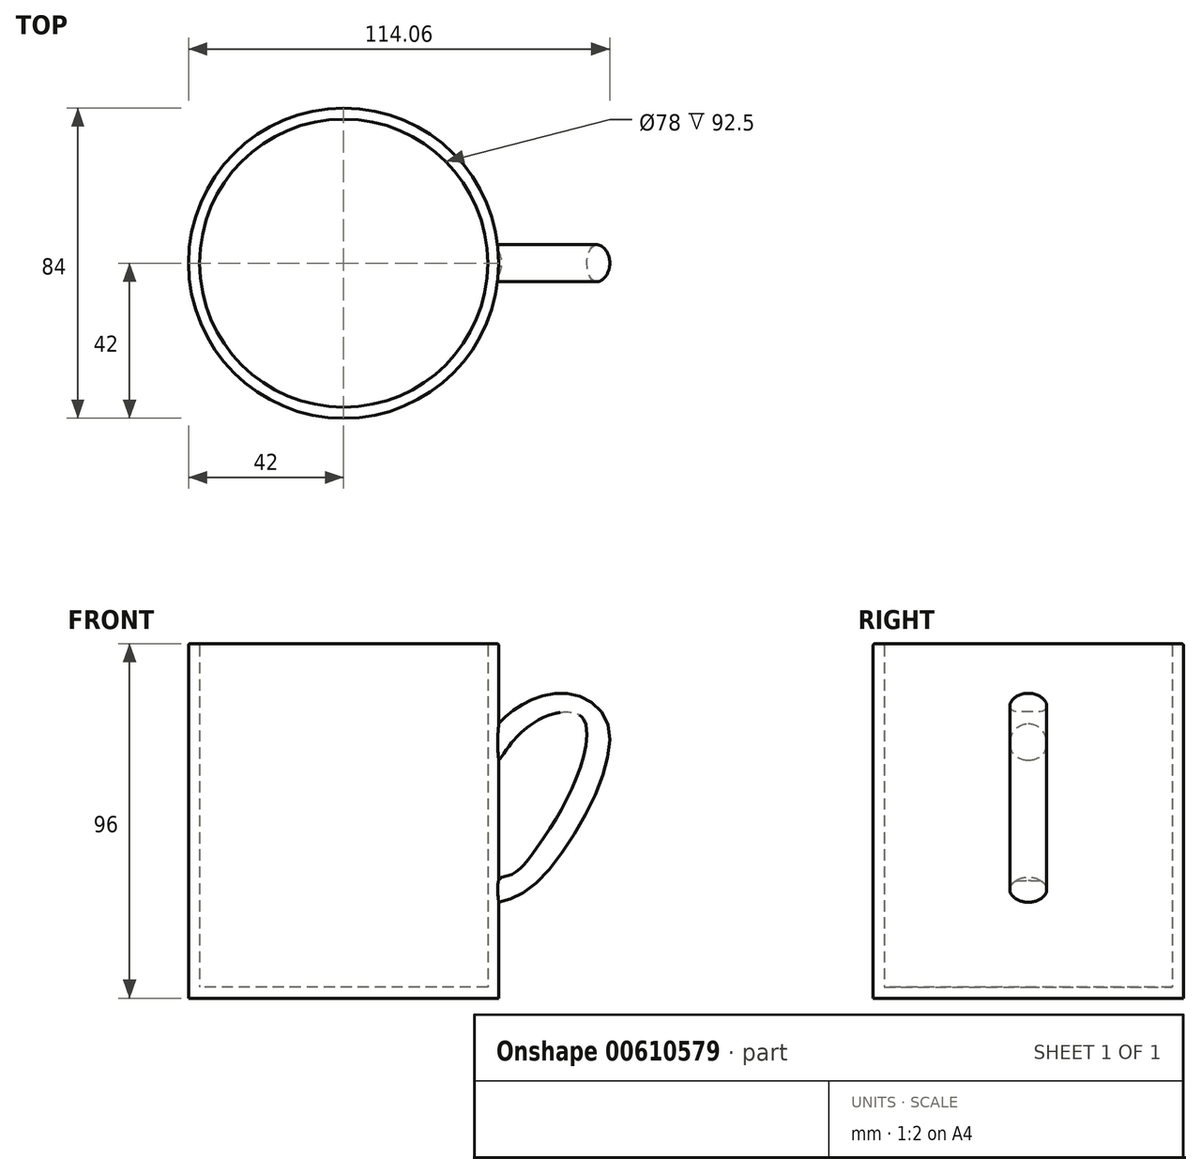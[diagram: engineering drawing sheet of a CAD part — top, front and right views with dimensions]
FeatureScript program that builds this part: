
annotation { "Feature Type Name" : "Feature", "Feature Type Description" : "" }
export const myFeature = defineFeature(function(context is Context, id is Id, definition is map)
    precondition{}
    {
        {
            var Q0;
            Q0=qCreatedBy(makeId("Top.planeOp"),FACE);
            var sketch = newSketch(context, id + "F0", { "sketchPlane" : qUnion([Q0])});
            skCircle(sketch, "E0", {"center": v(0, 0) * mm, "radius": 42 * mm});
            skSolve(sketch);
        }
        {
            var Q0;
            Q0 = qSketchRegion(id + "F0", true);
            extrude(context, id + "F1", {"entities" : qUnion([Q0]), "endBound" : BoundingType.SYMMETRIC, "depth" : 96 * mm, "offsetDistance" : 25 * mm});
        }
        {
            var Q0;
            Q0=qCreatedBy(makeId("Right.planeOp"),FACE);
            cPlane(context, id + "F2", {"entities" : qUnion([Q0]), "cplaneType" : CPlaneType.OFFSET, "offset" : 42 * mm, "width" : 150 * mm, "height" : 150 * mm});
        }
        {
            var Q0;
            Q0=qCreatedBy(makeId("Front.planeOp"),FACE);
            var sketch = newSketch(context, id + "F3", { "sketchPlane" : qUnion([Q0])});
            skFitSpline(sketch, "E1", {"points": [v(40.37, 21.1) * mm, v(47.45, 28.19) * mm, v(59.63, 32.15) * mm, v(69.54, 23.65) * mm, v(51.13, -14.59) * mm, v(38.38, -20.25) * mm], "startDerivative": vector(40.62, 48.6) * mm, "endDerivative": vector(-65.26, -9.16) * mm});
            skSolve(sketch);
        }
        {
            var Q0;
            Q0=qCreatedBy(id+"F2.planeOp",FACE);
            var sketch = newSketch(context, id + "F4", { "sketchPlane" : qUnion([Q0])});
            skCircle(sketch, "E2", {"center": v(0, 21.36) * mm, "radius": 5 * mm});
            skSolve(sketch);
        }
        {
            var Q0;
            Q0=makeQuery(id+"F4.imprint","IMPRINT",FACE,{"disambiguationData":[TD([[makeQuery(id+"F4.imprint","IMPRINT",EDGE,{"derivedFrom":sQuery(id+"F4.wireOp",EDGE,"E2")}),1.0]])]});
            var Q1;
            Q1=sQuery(id+"F3.wireOp",EDGE,"E1");
            sweep(context, id + "F5", {"operationType" : NewBodyOperationType.ADD, "profiles" : qUnion([Q0]), "path" : qUnion([Q1])});
        }
        {
            var Q0;
            Q0=makeQuery(id+"F1.opExtrude","CAP_FACE",FACE,{"disambiguationData":[OSD([sQuery(id+"F0.wireOp",EDGE,"E0")])],"isStart":false});
            shell(context, id + "F6", {"entities" : qUnion([Q0]), "thickness" : 3 * mm});
        }
        {
            var Q0;
            Q0=makeQuery(id+"F1.opExtrude","CAP_EDGE",EDGE,{"disambiguationData":[OSD([sQuery(id+"F0.wireOp",EDGE,"E0")])],"isStart":false});
            var Q1;
            {var subQ0=sQuery(id+"F0.wireOp",EDGE,"E0");Q1=makeQuery(id+"F6.opShell","OFFSET_EDGE",EDGE,{"disambiguationData":[OSD([subQ0]),TDD([makeQuery(id+"F1.opExtrude","CAP_EDGE",EDGE,{"disambiguationData":[OSD([subQ0])],"isStart":false})])]});}
            fillet(context, id + "F7", {"entities" : qUnion([Q0, Q1]), "radius" : 0.5 * mm, "tangentPropagation" : true, "allowEdgeOverflow" : false});
        }
    });
